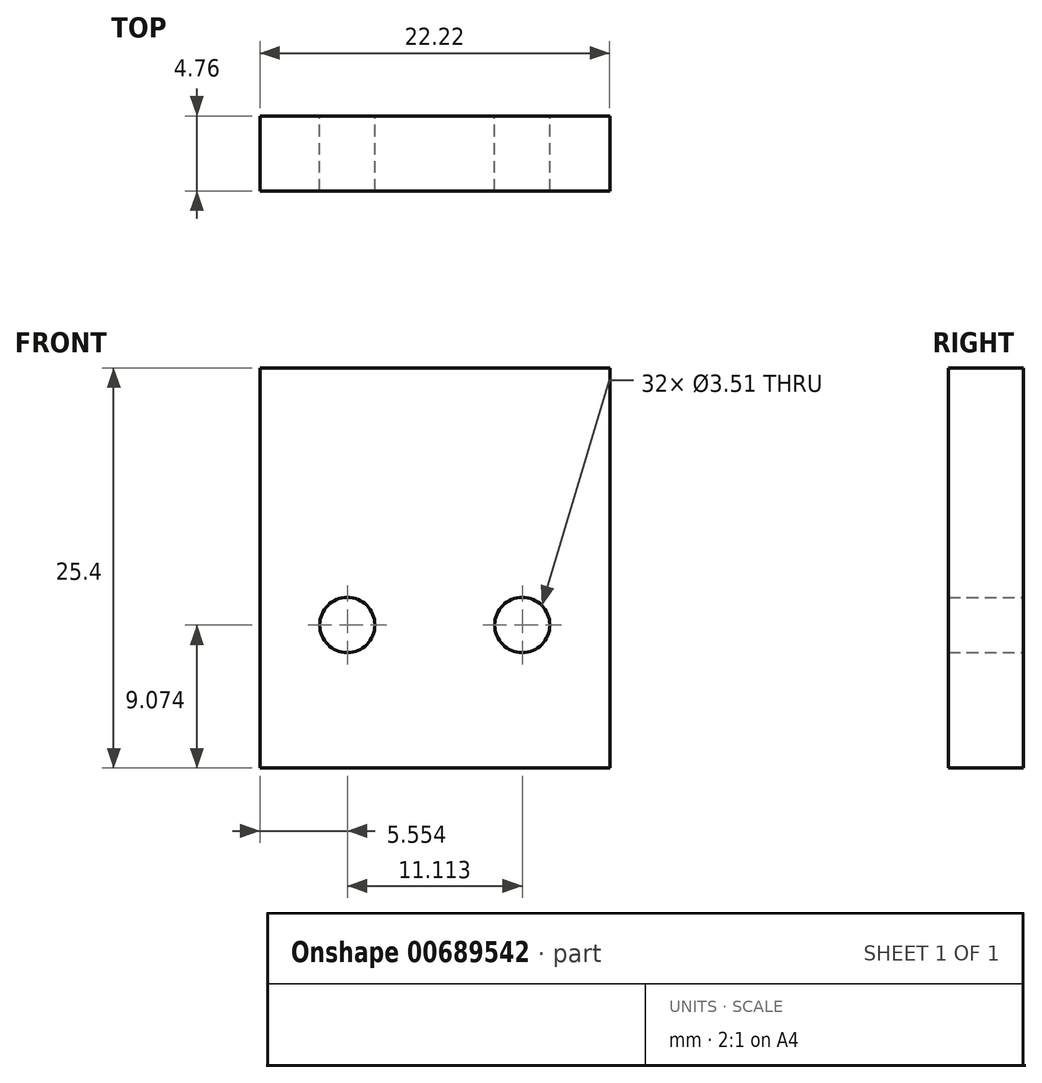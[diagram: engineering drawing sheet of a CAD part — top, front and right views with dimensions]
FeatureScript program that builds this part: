
annotation { "Feature Type Name" : "Feature", "Feature Type Description" : "" }
export const myFeature = defineFeature(function(context is Context, id is Id, definition is map)
    precondition{}
    {
        {
            var Q0;
            Q0=qCreatedBy(makeId("Front.planeOp"),FACE);
            var sketch = newSketch(context, id + "F0", { "sketchPlane" : qUnion([Q0])});
            skLineSegment(sketch, "E0.bottom", {"start": v(-11.11, 25.4) * mm, "end": v(11.11, 25.4) * mm});
            skLineSegment(sketch, "E0.top", {"start": v(-11.11, 0) * mm, "end": v(11.11, 0) * mm});
            skLineSegment(sketch, "E0.left", {"start": v(-11.11, 25.4) * mm, "end": v(-11.11, 0) * mm});
            skLineSegment(sketch, "E0.right", {"start": v(11.11, 25.4) * mm, "end": v(11.11, 0) * mm});
            skCircle(sketch, "E1", {"center": v(-5.56, 9.07) * mm, "radius": 1.75 * mm});
            skCircle(sketch, "E2", {"center": v(5.56, 9.07) * mm, "radius": 1.75 * mm});
            skSolve(sketch);
        }
        {
            var Q0;
            Q0 = qSketchRegion(id + "F0", true);
            extrude(context, id + "F1", {"entities" : qUnion([Q0]), "depth" : 4.76 * mm, "offsetDistance" : 25.4 * mm});
        }
    });
